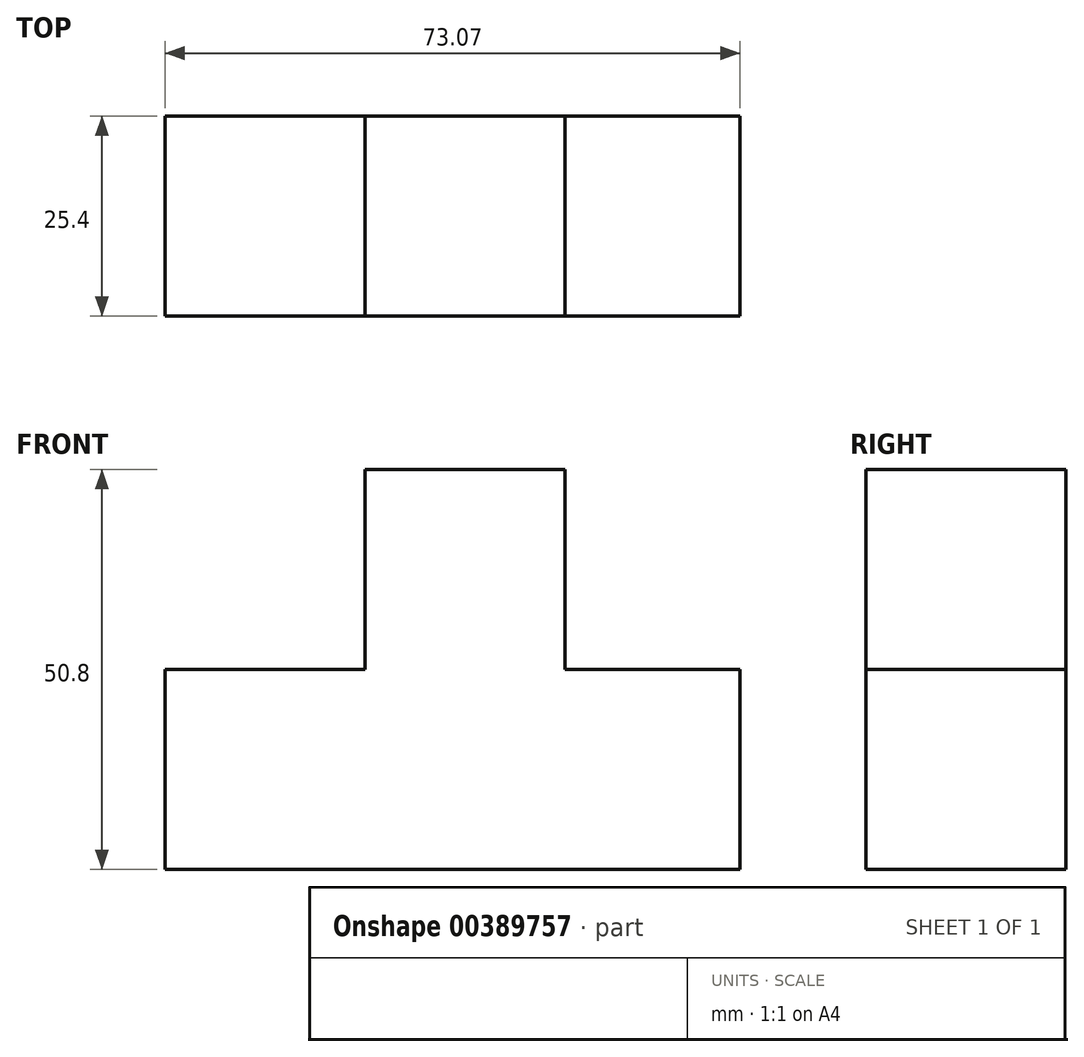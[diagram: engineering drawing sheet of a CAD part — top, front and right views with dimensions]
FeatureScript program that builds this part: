
annotation { "Feature Type Name" : "Feature", "Feature Type Description" : "" }
export const myFeature = defineFeature(function(context is Context, id is Id, definition is map)
    precondition{}
    {
        {
            var Q0;
            Q0=qCreatedBy(makeId("Front.planeOp"),FACE);
            var sketch = newSketch(context, id + "F0", { "sketchPlane" : qUnion([Q0])});
            skLineSegment(sketch, "E0.bottom", {"start": v(0, 0) * mm, "end": v(73.07, 0) * mm});
            skLineSegment(sketch, "E0.top", {"start": v(0, 25.4) * mm, "end": v(73.07, 25.4) * mm});
            skLineSegment(sketch, "E0.left", {"start": v(0, 0) * mm, "end": v(0, 25.4) * mm});
            skLineSegment(sketch, "E0.right", {"start": v(73.07, 0) * mm, "end": v(73.07, 25.4) * mm});
            skLineSegment(sketch, "E1.bottom", {"start": v(25.4, 25.4) * mm, "end": v(50.8, 25.4) * mm});
            skLineSegment(sketch, "E1.top", {"start": v(25.4, 50.8) * mm, "end": v(50.8, 50.8) * mm});
            skLineSegment(sketch, "E1.left", {"start": v(25.4, 25.4) * mm, "end": v(25.4, 50.8) * mm});
            skLineSegment(sketch, "E1.right", {"start": v(50.8, 25.4) * mm, "end": v(50.8, 50.8) * mm});
            skSolve(sketch);
        }
        {
            var Q0;
            Q0 = qSketchRegion(id + "F0", true);
            extrude(context, id + "F1", {"entities" : qUnion([Q0]), "depth" : 25.4 * mm});
        }
    });
